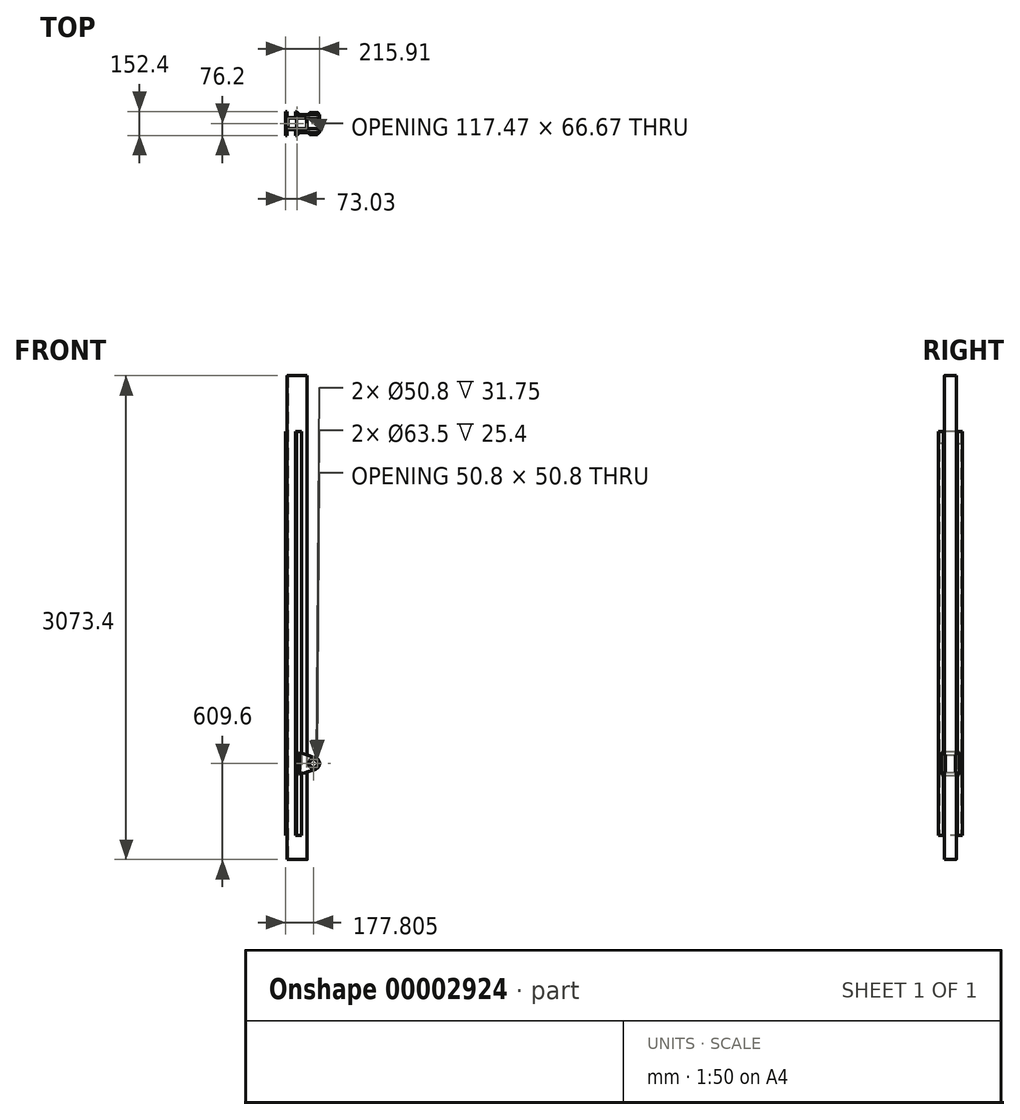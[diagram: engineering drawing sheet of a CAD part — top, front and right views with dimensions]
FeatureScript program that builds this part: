
annotation { "Feature Type Name" : "Feature", "Feature Type Description" : "" }
export const myFeature = defineFeature(function(context is Context, id is Id, definition is map)
    precondition{}
    {
        {
            var Q0;
            Q0=qCreatedBy(makeId("Top.planeOp"),FACE);
            var sketch = newSketch(context, id + "F0", { "sketchPlane" : qUnion([Q0])});
            skLineSegment(sketch, "E0.rect.bottom", {"start": v(-57.15, 38.1) * mm, "end": v(57.15, 38.1) * mm});
            skLineSegment(sketch, "E0.rect.top", {"start": v(-57.15, -38.1) * mm, "end": v(57.15, -38.1) * mm});
            skLineSegment(sketch, "E0.rect.left", {"start": v(-63.5, 31.75) * mm, "end": v(-63.5, -31.75) * mm});
            skLineSegment(sketch, "E0.rect.right", {"start": v(63.5, 31.75) * mm, "end": v(63.5, -31.75) * mm});
            skPoint(sketch, "E0.rect.middle", {"position": v(0, 0) * mm});
            skPoint(sketch, "E1.visualSharp", {"position": v(63.5, -38.1) * mm});
            skArc(sketch, "E1.filletArc", {"start": v(57.15, -38.1) * mm, "mid": v(61.64, -36.24) * mm, "end": v(63.5, -31.75) * mm});
            skPoint(sketch, "E2.visualSharp", {"position": v(63.5, 38.1) * mm});
            skArc(sketch, "E2.filletArc", {"start": v(63.5, 31.75) * mm, "mid": v(61.64, 36.24) * mm, "end": v(57.15, 38.1) * mm});
            skPoint(sketch, "E3.visualSharp", {"position": v(-63.5, -38.1) * mm});
            skArc(sketch, "E3.filletArc", {"start": v(-63.5, -31.75) * mm, "mid": v(-61.64, -36.24) * mm, "end": v(-57.15, -38.1) * mm});
            skPoint(sketch, "E4.visualSharp", {"position": v(-63.5, 38.1) * mm});
            skArc(sketch, "E4.filletArc", {"start": v(-57.15, 38.1) * mm, "mid": v(-61.64, 36.24) * mm, "end": v(-63.5, 31.75) * mm});
            skArc(sketch, "E5.0", {"start": v(58.74, 31.75) * mm, "mid": v(58.27, 32.87) * mm, "end": v(57.15, 33.34) * mm});
            skLineSegment(sketch, "E5.1", {"start": v(-57.15, 33.34) * mm, "end": v(57.15, 33.34) * mm});
            skArc(sketch, "E5.2", {"start": v(-57.15, 33.34) * mm, "mid": v(-58.27, 32.87) * mm, "end": v(-58.74, 31.75) * mm});
            skLineSegment(sketch, "E5.3", {"start": v(-58.74, 31.75) * mm, "end": v(-58.74, -31.75) * mm});
            skArc(sketch, "E5.4", {"start": v(-58.74, -31.75) * mm, "mid": v(-58.27, -32.87) * mm, "end": v(-57.15, -33.34) * mm});
            skLineSegment(sketch, "E5.5", {"start": v(58.74, 31.75) * mm, "end": v(58.74, -31.75) * mm});
            skLineSegment(sketch, "E5.6", {"start": v(-57.15, -33.34) * mm, "end": v(57.15, -33.34) * mm});
            skArc(sketch, "E5.7", {"start": v(57.15, -33.34) * mm, "mid": v(58.27, -32.87) * mm, "end": v(58.74, -31.75) * mm});
            skSolve(sketch);
        }
        {
            var Q0;
            Q0=makeQuery(id+"F0.imprint","IMPRINT",FACE,{"disambiguationData":[TD([[makeQuery(id+"F0.imprint","IMPRINT",EDGE,{"derivedFrom":sQuery(id+"F0.wireOp",EDGE,"E0.rect.bottom")}),-1.0]])]});
            extrude(context, id + "F1", {"entities" : qUnion([Q0]), "depth" : 3073.4 * mm});
        }
        {
            var Q0;
            Q0=makeQuery(id+"F1.opExtrude","SWEPT_FACE",FACE,{"disambiguationData":[OSD([sQuery(id+"F0.wireOp",EDGE,"E0.rect.left")])]});
            var sketch = newSketch(context, id + "F2", { "sketchPlane" : qUnion([Q0])});
            skLineSegment(sketch, "E6", {"start": v(0, 0) * mm, "end": v(0, 354.59) * mm, "construction": true});
            skLineSegment(sketch, "E7.rect.top", {"start": v(-76.2, 152.4) * mm, "end": v(76.2, 152.4) * mm});
            skLineSegment(sketch, "E7.rect.left", {"start": v(-76.2, 2641.6) * mm, "end": v(-76.2, 152.4) * mm});
            skLineSegment(sketch, "E7.rect.right", {"start": v(76.2, 2641.6) * mm, "end": v(76.2, 152.4) * mm});
            skPoint(sketch, "E7.rect.middle", {"position": v(0, 1435.1) * mm});
            skLineSegment(sketch, "E8", {"start": v(-38.1, 2641.6) * mm, "end": v(-76.2, 2641.6) * mm});
            skPoint(sketch, "E9.orphan", {"position": v(-76.2, 2717.8) * mm});
            skLineSegment(sketch, "E10", {"start": v(-38.1, 2641.6) * mm, "end": v(-38.1, 2717.8) * mm});
            skLineSegment(sketch, "E11", {"start": v(-38.1, 2717.8) * mm, "end": v(38.1, 2717.8) * mm});
            skLineSegment(sketch, "E12", {"start": v(38.1, 2717.8) * mm, "end": v(38.1, 2641.6) * mm});
            skLineSegment(sketch, "E13", {"start": v(38.1, 2641.6) * mm, "end": v(76.2, 2641.6) * mm});
            skPoint(sketch, "E14.orphan", {"position": v(76.2, 2717.8) * mm});
            skSolve(sketch);
        }
        {
            var Q0;
            {var subQ4=sQuery(id+"F2.wireOp",EDGE,"E7.rect.right");Q0=makeQuery(id+"F2.imprint","IMPRINT",FACE,{"disambiguationData":[TD([[makeQuery(id+"F2.imprint","IMPRINT",EDGE,{"derivedFrom":subQ4}),-1.0]])]});}
            var Q1;
            {var subQ0=sQuery(id+"F0.wireOp",EDGE,"E0.rect.left");var subQ4=sQuery(id+"F2.wireOp",EDGE,"E7.rect.bottom");var subQ6=makeQuery(id+"F1.opExtrude","SWEPT_EDGE",EDGE,{"disambiguationData":[OSD([subQ0,sQuery(id+"F0.wireOp",EDGE,"E4.filletArc")])]});var subQ8=makeQuery(id+"F2.imprint","INTERSECT",VERTEX,{"derivedFrom":[subQ6,subQ4]});Q1=makeQuery(id+"F2.imprint","IMPRINT",FACE,{"disambiguationData":[TD([[makeQuery(id+"F2.imprint","IMPRINT",EDGE,{"disambiguationData":[TD([[subQ8,-1.0]])],"derivedFrom":subQ4}),-1.0]])]});}
            var Q2;
            {var subQ6=sQuery(id+"F2.wireOp",EDGE,"E7.rect.left");Q2=makeQuery(id+"F2.imprint","IMPRINT",FACE,{"disambiguationData":[TD([[makeQuery(id+"F2.imprint","IMPRINT",EDGE,{"derivedFrom":subQ6}),1.0]])]});}
            var Q3;
            {var subQ0=sQuery(id+"F0.wireOp",EDGE,"E0.rect.left");var subQ4=sQuery(id+"F2.wireOp",EDGE,"E7.rect.top");var subQ6=makeQuery(id+"F1.opExtrude","SWEPT_EDGE",EDGE,{"disambiguationData":[OSD([subQ0,sQuery(id+"F0.wireOp",EDGE,"E4.filletArc")])]});var subQ8=makeQuery(id+"F2.imprint","INTERSECT",VERTEX,{"derivedFrom":[subQ6,subQ4]});Q3=makeQuery(id+"F2.imprint","IMPRINT",FACE,{"disambiguationData":[TD([[makeQuery(id+"F2.imprint","IMPRINT",EDGE,{"disambiguationData":[TD([[subQ8,-1.0]])],"derivedFrom":subQ4}),1.0]])]});}
            extrude(context, id + "F3", {"entities" : qUnion([Q0, Q1, Q2, Q3]), "depth" : 9.52 * mm});
        }
        {
            var Q0;
            Q0=makeQuery(id+"F3.opExtrude","SWEPT_FACE",FACE,{"disambiguationData":[OSD([sQuery(id+"F2.wireOp",EDGE,"E7.rect.top")])]});
            var sketch = newSketch(context, id + "F4", { "sketchPlane" : qUnion([Q0])});
            skLineSegment(sketch, "E15", {"start": v(-9.52, 76.2) * mm, "end": v(-9.52, 38.1) * mm});
            skLineSegment(sketch, "E16", {"start": v(-9.52, 38.1) * mm, "end": v(28.58, 38.1) * mm});
            skLineSegment(sketch, "E17.0", {"start": v(-3.17, 44.45) * mm, "end": v(28.58, 44.45) * mm});
            skLineSegment(sketch, "E17.1", {"start": v(-3.17, 76.2) * mm, "end": v(-3.17, 44.45) * mm});
            skLineSegment(sketch, "E18", {"start": v(-9.52, 76.2) * mm, "end": v(-3.17, 76.2) * mm});
            skLineSegment(sketch, "E19", {"start": v(28.58, 44.45) * mm, "end": v(28.58, 38.1) * mm});
            skSolve(sketch);
        }
        {
            var Q0;
            Q0=makeQuery(id+"F4.imprint","IMPRINT",FACE,{"disambiguationData":[TD([[makeQuery(id+"F4.imprint","IMPRINT",EDGE,{"derivedFrom":sQuery(id+"F4.wireOp",EDGE,"E15")}),1.0]])]});
            extrude(context, id + "F5", {"entities" : qUnion([Q0]), "oppositeDirection" : true, "depth" : 2565.4 * mm});
        }
        {
            var Q0;
            Q0=makeQuery(id+"F5.opExtrude","SWEPT_BODY",BODY,{"disambiguationData":[OSD([sQuery(id+"F4.wireOp",EDGE,"E15"),sQuery(id+"F4.wireOp",EDGE,"E16"),sQuery(id+"F4.wireOp",EDGE,"E17.0"),sQuery(id+"F4.wireOp",EDGE,"E17.1"),sQuery(id+"F4.wireOp",EDGE,"E18"),sQuery(id+"F4.wireOp",EDGE,"E19")])]});
            var Q1;
            Q1=qCreatedBy(makeId("Front.planeOp"),FACE);
            mirror(context, id + "F6", {"entities" : qUnion([Q0]), "mirrorPlane" : qUnion([Q1])});
        }
        {
            var Q0;
            Q0=makeQuery(id+"F5.opExtrude","CAP_FACE",FACE,{"disambiguationData":[OSD([sQuery(id+"F4.wireOp",EDGE,"E15"),sQuery(id+"F4.wireOp",EDGE,"E16"),sQuery(id+"F4.wireOp",EDGE,"E17.0"),sQuery(id+"F4.wireOp",EDGE,"E17.1"),sQuery(id+"F4.wireOp",EDGE,"E18"),sQuery(id+"F4.wireOp",EDGE,"E19")])],"isStart":true});
            var sketch = newSketch(context, id + "F7", { "sketchPlane" : qUnion([Q0])});
            skLineSegment(sketch, "E20", {"start": v(-3.17, 76.2) * mm, "end": v(28.58, 44.45) * mm});
            skLineSegment(sketch, "E21.0", {"start": v(-3.17, 69.46) * mm, "end": v(21.84, 44.45) * mm});
            skLineSegment(sketch, "E22", {"start": v(-3.17, 76.2) * mm, "end": v(-3.17, 69.46) * mm});
            skLineSegment(sketch, "E23", {"start": v(21.84, 44.45) * mm, "end": v(28.58, 44.45) * mm});
            skSolve(sketch);
        }
        {
            var Q0;
            Q0=makeQuery(id+"F7.imprint","IMPRINT",FACE,{"disambiguationData":[TD([[makeQuery(id+"F7.imprint","IMPRINT",EDGE,{"derivedFrom":sQuery(id+"F7.wireOp",EDGE,"E20")}),-1.0]])]});
            extrude(context, id + "F8", {"entities" : qUnion([Q0]), "oppositeDirection" : true, "depth" : 2565.4 * mm});
        }
        {
            var Q0;
            Q0=makeQuery(id+"F8.opExtrude","SWEPT_BODY",BODY,{"disambiguationData":[OSD([sQuery(id+"F7.wireOp",EDGE,"E20"),sQuery(id+"F7.wireOp",EDGE,"E21.0"),sQuery(id+"F7.wireOp",EDGE,"E22"),sQuery(id+"F7.wireOp",EDGE,"E23")])]});
            var Q1;
            Q1=qCreatedBy(makeId("Front.planeOp"),FACE);
            mirror(context, id + "F9", {"entities" : qUnion([Q0]), "mirrorPlane" : qUnion([Q1])});
        }
        {
            var Q0;
            Q0=makeQuery(id+"F1.opExtrude","SWEPT_FACE",FACE,{"disambiguationData":[OSD([sQuery(id+"F0.wireOp",EDGE,"E0.rect.top")])]});
            var Q1;
            Q1=makeQuery(id+"F1.opExtrude","SWEPT_FACE",FACE,{"disambiguationData":[OSD([sQuery(id+"F0.wireOp",EDGE,"E0.rect.bottom")])]});
            cPlane(context, id + "F10", {"entities" : qUnion([Q0, Q1]), "cplaneType" : CPlaneType.MID_PLANE, "offset" : 152.4 * mm, "width" : 152.4 * mm, "height" : 152.4 * mm});
        }
        {
            var Q0;
            Q0=qCreatedBy(id+"F10.planeOp",FACE);
            var sketch = newSketch(context, id + "F11", { "sketchPlane" : qUnion([Q0])});
            skCircle(sketch, "E24", {"center": v(104.78, 609.6) * mm, "radius": 31.75 * mm});
            skCircle(sketch, "E25", {"center": v(104.78, 609.6) * mm, "radius": 25.4 * mm});
            skLineSegment(sketch, "E26", {"start": v(104.78, 609.6) * mm, "end": v(104.78, 366.8) * mm, "construction": true});
            skSolve(sketch);
        }
        {
            var Q0;
            Q0=makeQuery(id+"F11.imprint","IMPRINT",FACE,{"disambiguationData":[TD([[makeQuery(id+"F11.imprint","IMPRINT",EDGE,{"derivedFrom":sQuery(id+"F11.wireOp",EDGE,"E24")}),1.0]])]});
            extrude(context, id + "F12", {"entities" : qUnion([Q0]), "depth" : 127 * mm, "symmetric" : true});
        }
        {
            var Q0;
            Q0=makeQuery(id+"F11.imprint","IMPRINT",FACE,{"disambiguationData":[TD([[makeQuery(id+"F11.imprint","IMPRINT",EDGE,{"derivedFrom":sQuery(id+"F11.wireOp",EDGE,"E25")}),1.0]])]});
            extrude(context, id + "F13", {"entities" : qUnion([Q0]), "depth" : 139.7 * mm, "symmetric" : true});
        }
        {
            var Q0;
            Q0=makeQuery(id+"F12.opExtrude","CAP_FACE",FACE,{"disambiguationData":[OSD([sQuery(id+"F11.wireOp",EDGE,"E24"),sQuery(id+"F11.wireOp",EDGE,"E25")])],"isStart":true});
            cPlane(context, id + "F14", {"entities" : qUnion([Q0]), "cplaneType" : CPlaneType.OFFSET, "offset" : 6.35 * mm, "oppositeDirection" : true, "width" : 152.4 * mm, "height" : 152.4 * mm});
        }
        {
            var Q0;
            Q0=qCreatedBy(id+"F14.planeOp",FACE);
            var sketch = newSketch(context, id + "F15", { "sketchPlane" : qUnion([Q0])});
            skCircle(sketch, "E27.0", {"center": v(-104.78, 609.6) * mm, "radius": 31.75 * mm});
            skLineSegment(sketch, "E28.0", {"start": v(3.17, 2717.8) * mm, "end": v(3.17, 152.4) * mm});
            skCircle(sketch, "E29.0", {"center": v(-104.78, 609.6) * mm, "radius": 38.1 * mm});
            skLineSegment(sketch, "E30", {"start": v(-104.78, 609.6) * mm, "end": v(3.17, 609.6) * mm});
            skLineSegment(sketch, "E31", {"start": v(3.17, 533.4) * mm, "end": v(-116.84, 573.46) * mm});
            skLineSegment(sketch, "E32", {"start": v(3.17, 685.8) * mm, "end": v(-116.84, 645.74) * mm});
            skLineSegment(sketch, "E33", {"start": v(3.17, 533.4) * mm, "end": v(3.17, 685.8) * mm});
            skSolve(sketch);
        }
        {
            var Q0;
            {var subQ1=sQuery(id+"F15.wireOp",EDGE,"E31");Q0=makeQuery(id+"F15.imprint","IMPRINT",FACE,{"disambiguationData":[TD([[makeQuery(id+"F15.imprint","IMPRINT",EDGE,{"derivedFrom":subQ1}),-1.0]])]});}
            var Q1;
            {var subQ1=sQuery(id+"F15.wireOp",EDGE,"E32");Q1=makeQuery(id+"F15.imprint","IMPRINT",FACE,{"disambiguationData":[TD([[makeQuery(id+"F15.imprint","IMPRINT",EDGE,{"derivedFrom":subQ1}),1.0]])]});}
            var Q2;
            {var subQ3=sQuery(id+"F15.wireOp",EDGE,"E27.0");Q2=makeQuery(id+"F15.imprint","IMPRINT",FACE,{"disambiguationData":[TD([[makeQuery(id+"F15.imprint","IMPRINT",EDGE,{"derivedFrom":subQ3}),-1.0]])]});}
            extrude(context, id + "F16", {"entities" : qUnion([Q0, Q1, Q2]), "oppositeDirection" : true, "depth" : 114.3 * mm});
        }
        {
            var Q0;
            Q0=makeQuery(id+"F1.opExtrude","SWEPT_BODY",BODY,{"disambiguationData":[OSD([sQuery(id+"F0.wireOp",EDGE,"E0.rect.bottom"),sQuery(id+"F0.wireOp",EDGE,"E0.rect.top"),sQuery(id+"F0.wireOp",EDGE,"E0.rect.left"),sQuery(id+"F0.wireOp",EDGE,"E0.rect.right"),sQuery(id+"F0.wireOp",EDGE,"E1.filletArc"),sQuery(id+"F0.wireOp",EDGE,"E2.filletArc"),sQuery(id+"F0.wireOp",EDGE,"E3.filletArc"),sQuery(id+"F0.wireOp",EDGE,"E4.filletArc"),sQuery(id+"F0.wireOp",EDGE,"E5.0"),sQuery(id+"F0.wireOp",EDGE,"E5.1"),sQuery(id+"F0.wireOp",EDGE,"E5.2"),sQuery(id+"F0.wireOp",EDGE,"E5.3"),sQuery(id+"F0.wireOp",EDGE,"E5.4"),sQuery(id+"F0.wireOp",EDGE,"E5.5"),sQuery(id+"F0.wireOp",EDGE,"E5.6"),sQuery(id+"F0.wireOp",EDGE,"E5.7")])]});
            var Q1;
            Q1=makeQuery(id+"F9.opPattern","COPY",BODY,{"derivedFrom":makeQuery(id+"F8.opExtrude","SWEPT_BODY",BODY,{"disambiguationData":[OSD([sQuery(id+"F7.wireOp",EDGE,"E20"),sQuery(id+"F7.wireOp",EDGE,"E21.0"),sQuery(id+"F7.wireOp",EDGE,"E22"),sQuery(id+"F7.wireOp",EDGE,"E23")])]}),"instanceName":"1"});
            var Q2;
            Q2=makeQuery(id+"F8.opExtrude","SWEPT_BODY",BODY,{"disambiguationData":[OSD([sQuery(id+"F7.wireOp",EDGE,"E20"),sQuery(id+"F7.wireOp",EDGE,"E21.0"),sQuery(id+"F7.wireOp",EDGE,"E22"),sQuery(id+"F7.wireOp",EDGE,"E23")])]});
            var Q3;
            Q3=makeQuery(id+"F16.opExtrude","SWEPT_BODY",BODY,{"disambiguationData":[OSD([sQuery(id+"F15.wireOp",EDGE,"E27.0"),sQuery(id+"F15.wireOp",EDGE,"E29.0"),sQuery(id+"F15.wireOp",EDGE,"E31"),sQuery(id+"F15.wireOp",EDGE,"E32"),sQuery(id+"F15.wireOp",EDGE,"E33")])]});
            booleanBodies(context, id + "F17", {"operationType" : BooleanOperationType.SUBTRACTION, "tools" : qUnion([Q0, Q1, Q2]), "targets" : qUnion([Q3]), "keepTools" : true});
        }
        {
            var Q0;
            Q0=makeQuery(id+"F1.opExtrude","SWEPT_FACE",FACE,{"disambiguationData":[OSD([sQuery(id+"F0.wireOp",EDGE,"E0.rect.right")])]});
            var sketch = newSketch(context, id + "F18", { "sketchPlane" : qUnion([Q0])});
            skLineSegment(sketch, "E34.bottom", {"start": v(38.1, 502.42) * mm, "end": v(-38.1, 502.42) * mm});
            skLineSegment(sketch, "E34.top", {"start": v(38.1, 702.22) * mm, "end": v(-38.1, 702.22) * mm});
            skLineSegment(sketch, "E34.left", {"start": v(38.1, 502.42) * mm, "end": v(38.1, 702.22) * mm});
            skLineSegment(sketch, "E34.right", {"start": v(-38.1, 502.42) * mm, "end": v(-38.1, 702.22) * mm});
            skSolve(sketch);
        }
        {
            var Q0;
            {var subQ0=sQuery(id+"F0.wireOp",EDGE,"E0.rect.right");var subQ4=sQuery(id+"F18.wireOp",EDGE,"E34.bottom");var subQ6=makeQuery(id+"F1.opExtrude","SWEPT_EDGE",EDGE,{"disambiguationData":[OSD([subQ0,sQuery(id+"F0.wireOp",EDGE,"E2.filletArc")])]});var subQ8=makeQuery(id+"F18.imprint","INTERSECT",VERTEX,{"derivedFrom":[subQ6,subQ4]});Q0=makeQuery(id+"F18.imprint","IMPRINT",FACE,{"disambiguationData":[TD([[makeQuery(id+"F18.imprint","IMPRINT",EDGE,{"disambiguationData":[TD([[subQ8,-1.0]])],"derivedFrom":subQ4}),-1.0]])]});}
            extrude(context, id + "F19", {"entities" : qUnion([Q0]), "operationType" : NewBodyOperationType.REMOVE, "depth" : 121.56 * mm});
        }
    });
